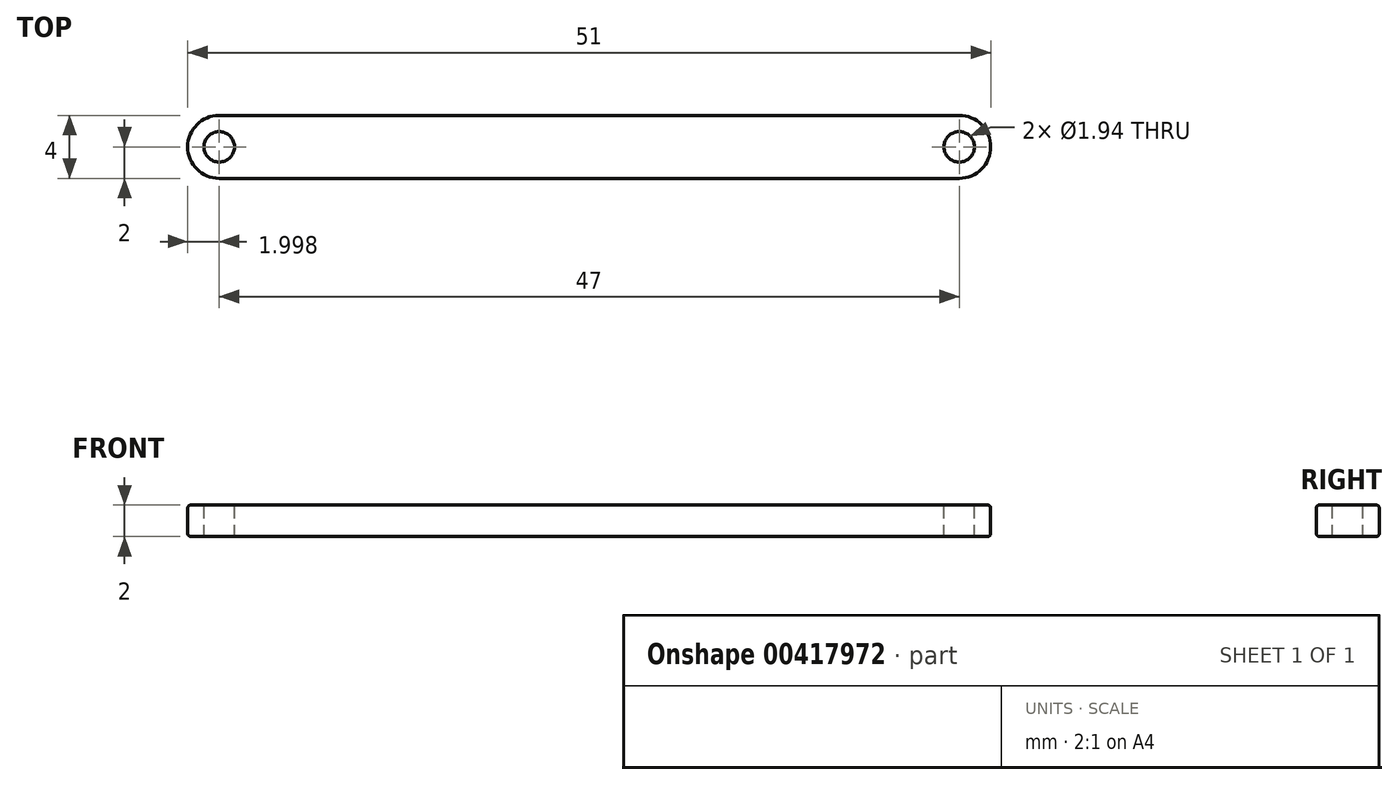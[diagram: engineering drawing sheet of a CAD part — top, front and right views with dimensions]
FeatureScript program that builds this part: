
annotation { "Feature Type Name" : "Feature", "Feature Type Description" : "" }
export const myFeature = defineFeature(function(context is Context, id is Id, definition is map)
    precondition{}
    {
        {
            var Q0;
            Q0=qCreatedBy(makeId("Top.planeOp"),FACE);
            var sketch = newSketch(context, id + "F0", { "sketchPlane" : qUnion([Q0])});
            skLineSegment(sketch, "E0.bottom", {"start": v(-22.77, -1.94) * mm, "end": v(28.23, -1.94) * mm});
            skLineSegment(sketch, "E0.top", {"start": v(-22.77, -5.94) * mm, "end": v(28.23, -5.94) * mm});
            skLineSegment(sketch, "E0.left", {"start": v(-22.77, -1.94) * mm, "end": v(-22.77, -5.94) * mm});
            skLineSegment(sketch, "E0.right", {"start": v(28.23, -1.94) * mm, "end": v(28.23, -5.94) * mm});
            skSolve(sketch);
        }
        {
            var Q0;
            Q0 = qSketchRegion(id + "F0", true);
            extrude(context, id + "F1", {"entities" : qUnion([Q0]), "depth" : 2 * mm});
        }
        {
            var Q0;
            Q0=makeQuery(id+"F1.opExtrude","SWEPT_EDGE",EDGE,{"disambiguationData":[OSD([sQuery(id+"F0.wireOp",EDGE,"E0.bottom"),sQuery(id+"F0.wireOp",EDGE,"E0.right")])]});
            var Q1;
            Q1=makeQuery(id+"F1.opExtrude","SWEPT_EDGE",EDGE,{"disambiguationData":[OSD([sQuery(id+"F0.wireOp",EDGE,"E0.top"),sQuery(id+"F0.wireOp",EDGE,"E0.right")])]});
            var Q2;
            Q2=makeQuery(id+"F1.opExtrude","SWEPT_EDGE",EDGE,{"disambiguationData":[OSD([sQuery(id+"F0.wireOp",EDGE,"E0.bottom"),sQuery(id+"F0.wireOp",EDGE,"E0.left")])]});
            var Q3;
            Q3=makeQuery(id+"F1.opExtrude","SWEPT_EDGE",EDGE,{"disambiguationData":[OSD([sQuery(id+"F0.wireOp",EDGE,"E0.top"),sQuery(id+"F0.wireOp",EDGE,"E0.left")])]});
            fillet(context, id + "F2", {"entities" : qUnion([Q0, Q1, Q2, Q3]), "radius" : 2 * mm, "tangentPropagation" : true, "allowEdgeOverflow" : false});
        }
        {
            var Q0;
            Q0=makeQuery(id+"F1.opExtrude","CAP_FACE",FACE,{"disambiguationData":[OSD([sQuery(id+"F0.wireOp",EDGE,"E0.bottom"),sQuery(id+"F0.wireOp",EDGE,"E0.top"),sQuery(id+"F0.wireOp",EDGE,"E0.left"),sQuery(id+"F0.wireOp",EDGE,"E0.right")])],"isStart":false});
            var sketch = newSketch(context, id + "F3", { "sketchPlane" : qUnion([Q0])});
            skCircle(sketch, "E1", {"center": v(-20.77, -3.94) * mm, "radius": 0.97 * mm});
            skCircle(sketch, "E2", {"center": v(26.23, -3.94) * mm, "radius": 0.97 * mm});
            skSolve(sketch);
        }
        {
            var Q0;
            Q0 = qSketchRegion(id + "F3", true);
            extrude(context, id + "F4", {"entities" : qUnion([Q0]), "operationType" : NewBodyOperationType.REMOVE, "oppositeDirection" : true, "depth" : 25 * mm});
        }
        {
            var Q0;
            Q0=makeQuery(id+"F1.opExtrude","CAP_EDGE",EDGE,{"disambiguationData":[OSD([sQuery(id+"F0.wireOp",EDGE,"E0.bottom")])],"isStart":true});
            var Q1;
            Q1=makeQuery(id+"F1.opExtrude","CAP_EDGE",EDGE,{"disambiguationData":[OSD([sQuery(id+"F0.wireOp",EDGE,"E0.top")])],"isStart":false});
            fillet(context, id + "F5", {"entities" : qUnion([Q0, Q1]), "radius" : 0.2 * mm, "tangentPropagation" : true, "allowEdgeOverflow" : false});
        }
    });
